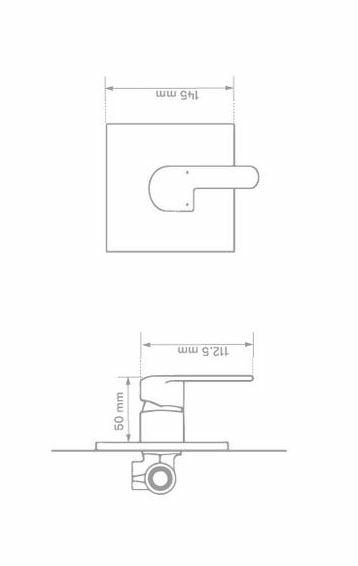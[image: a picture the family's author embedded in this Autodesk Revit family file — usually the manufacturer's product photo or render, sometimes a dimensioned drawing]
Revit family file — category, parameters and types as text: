
# Revit family: 01-1634-11 CONJUNTO REGISTRO DUCHA HELIX CRUZ
name_source: partatom
category: Plumbing Fixtures
revit_build: Autodesk Revit 2018 (Build: 20170223_1515(x64)
units: mm (PartAtom-declared; Revit-internal decimal feet)

## family parameters
Cut with Voids When Loaded = No
Host = Face
OmniClass Number = 23.31.11.00
Part Type = Normal
Room Calculation Point = No
Round Connector Dimension = Use Diameter
Shared = No

## types (1)
- 01-1634-11
    Alto manija = 85 mm  [stored 0.278871 ft]
    Ancho manija = 66 mm
    CW Connection = Yes
    Default Elevation = 0 mm  [stored 0 ft]
    Description = Mezclador ducha
    Escudo = 60 mm  [stored 0.19685 ft]
    Ficha tecnica = No encontrada en internet
    HW Connection = Yes
    Laton = Laton
    Manufacturer = Gricol
    Metal Laton Cromado = Metal Laton Cromado
    Model = 01-1634-11
    Plastico - ABS Cromado = Plastico ABS Cromado
    Product Name = CONJUNTO REGISTRO DUCHA HELIX CRUZ
    Sepacion entre registro y ducha = 400 mm  [stored 1.31234 ft]
    Type Image = LOGO-01.jpg
    URL = https://www.gricol.com
    Vent Connection = No
    Waste Connection = No

note: [stored X ft] marks values corroborated as IEEE doubles in the binary element streams (Revit-internal decimal feet)

## geometry (parser evidence)
native form markers: Blend x4, Sweep x25
no freeform markers — native parametric forms only
